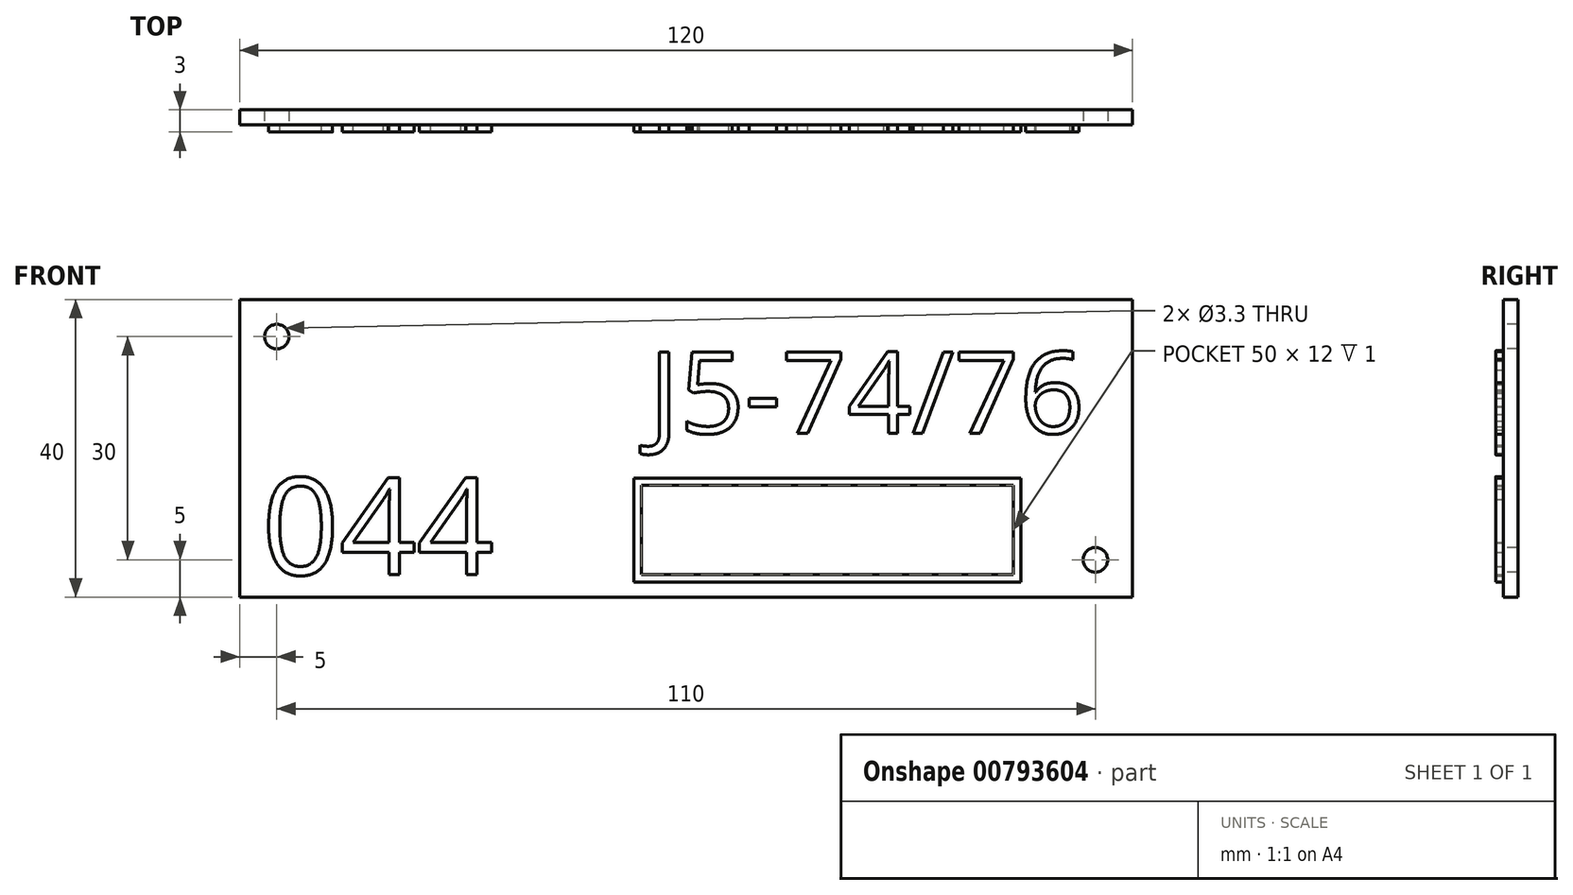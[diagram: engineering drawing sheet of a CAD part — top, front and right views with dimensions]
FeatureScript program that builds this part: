
annotation { "Feature Type Name" : "Feature", "Feature Type Description" : "" }
export const myFeature = defineFeature(function(context is Context, id is Id, definition is map)
    precondition{}
    {
        {
            var Q0;
            Q0=qCreatedBy(makeId("Front.planeOp"),FACE);
            var sketch = newSketch(context, id + "F0", { "sketchPlane" : qUnion([Q0])});
            skLineSegment(sketch, "E0.bottom", {"start": v(60, -20) * mm, "end": v(-60, -20) * mm});
            skLineSegment(sketch, "E0.top", {"start": v(60, 20) * mm, "end": v(-60, 20) * mm});
            skLineSegment(sketch, "E0.left", {"start": v(60, -20) * mm, "end": v(60, 20) * mm});
            skLineSegment(sketch, "E0.right", {"start": v(-60, -20) * mm, "end": v(-60, 20) * mm});
            skPoint(sketch, "E0.middle", {"position": v(0, 0) * mm});
            skSolve(sketch);
        }
        {
            var Q0;
            Q0=makeQuery(id+"F0.imprint","IMPRINT",FACE,{"disambiguationData":[TD([[makeQuery(id+"F0.imprint","IMPRINT",EDGE,{"derivedFrom":sQuery(id+"F0.wireOp",EDGE,"E0.bottom")}),-1.0]])]});
            extrude(context, id + "F1", {"entities" : qUnion([Q0]), "depth" : 2 * mm});
        }
        {
            var Q0;
            Q0=makeQuery(id+"F1.opExtrude","CAP_FACE",FACE,{"disambiguationData":[OSD([sQuery(id+"F0.wireOp",EDGE,"E0.bottom"),sQuery(id+"F0.wireOp",EDGE,"E0.top"),sQuery(id+"F0.wireOp",EDGE,"E0.left"),sQuery(id+"F0.wireOp",EDGE,"E0.right")])],"isStart":false});
            var sketch = newSketch(context, id + "F2", { "sketchPlane" : qUnion([Q0])});
            skPoint(sketch, "E1", {"position": v(-55, 15) * mm});
            skPoint(sketch, "E2", {"position": v(55, -15) * mm});
            skSolve(sketch);
        }
        {
            var Q0;
            Q0=sQuery(id+"F2.wireOp",VERTEX,"E1");
            var Q1;
            Q1=sQuery(id+"F2.wireOp",VERTEX,"E2");
            var Q2;
            Q2=makeQuery(id+"F1.opExtrude","SWEPT_BODY",BODY,{"disambiguationData":[OSD([sQuery(id+"F0.wireOp",EDGE,"E0.bottom"),sQuery(id+"F0.wireOp",EDGE,"E0.top"),sQuery(id+"F0.wireOp",EDGE,"E0.left"),sQuery(id+"F0.wireOp",EDGE,"E0.right")])]});
            hole(context, id + "F3", {"style" : HoleStyle.SIMPLE, "endStyle" : HoleEndStyle.THROUGH, "holeDiameter" : 3.3 * mm, "locations" : qUnion([Q0, Q1]), "scope" : qUnion([Q2]), "isTappedThrough" : true});
        }
        {
            var Q0;
            Q0=makeQuery(id+"F1.opExtrude","CAP_FACE",FACE,{"disambiguationData":[OSD([sQuery(id+"F0.wireOp",EDGE,"E0.bottom"),sQuery(id+"F0.wireOp",EDGE,"E0.top"),sQuery(id+"F0.wireOp",EDGE,"E0.left"),sQuery(id+"F0.wireOp",EDGE,"E0.right")])],"isStart":false});
            var sketch = newSketch(context, id + "F4", { "sketchPlane" : qUnion([Q0])});
            skText(sketch, "E3", { "text": "J5-74/76", "fontName": "OpenSans-Regular.ttf"});
            const initialGuessF4  = {"E3": [-0.005, 0.002, 1, 0, 0.01105]};
            skSetInitialGuess(sketch, initialGuessF4);
            skSolve(sketch);
        }
        {
            var Q0;
            Q0=qSketchRegion(id+"F4",true);
            extrude(context, id + "F5", {"entities" : qUnion([Q0]), "operationType" : NewBodyOperationType.ADD, "depth" : 1 * mm});
        }
        {
            var Q0;
            {var subQ0=sQuery(id+"F0.wireOp",EDGE,"E0.top");var subQ1=sQuery(id+"F0.wireOp",EDGE,"E0.left");var subQ2=sQuery(id+"F0.wireOp",EDGE,"E0.right");var subQ3=sQuery(id+"F0.wireOp",EDGE,"E0.bottom");Q0=makeQuery(id+"F5.boolean.opBoolean","SPLIT",FACE,{"disambiguationData":[TD([makeQuery(id+"F1.opExtrude","SWEPT_FACE",FACE,{"disambiguationData":[OSD([subQ3])]})])],"derivedFrom":makeQuery(id+"F1.opExtrude","CAP_FACE",FACE,{"disambiguationData":[OSD([subQ3,subQ0,subQ1,subQ2])],"isStart":false})});}
            var sketch = newSketch(context, id + "F6", { "sketchPlane" : qUnion([Q0])});
            skText(sketch, "E4", { "text": "044", "fontName": "OpenSans-Regular.ttf"});
            const initialGuessF6  = {"E4": [-0.057, -0.017, 1, 0, 0.0131]};
            skSetInitialGuess(sketch, initialGuessF6);
            skSolve(sketch);
        }
        {
            var Q0;
            Q0=qSketchRegion(id+"F6",true);
            extrude(context, id + "F7", {"entities" : qUnion([Q0]), "operationType" : NewBodyOperationType.ADD, "depth" : 1 * mm});
        }
        {
            var Q0;
            {var subQ46=sQuery(id+"F0.wireOp",EDGE,"E0.top");var subQ48=sQuery(id+"F0.wireOp",EDGE,"E0.left");var subQ66=sQuery(id+"F0.wireOp",EDGE,"E0.right");var subQ76=sQuery(id+"F0.wireOp",EDGE,"E0.bottom");var subQ77=makeQuery(id+"F1.opExtrude","SWEPT_FACE",FACE,{"disambiguationData":[OSD([subQ76])]});Q0=makeQuery(id+"F7.boolean.opBoolean","SPLIT",FACE,{"disambiguationData":[TD([subQ77])],"derivedFrom":makeQuery(id+"F5.boolean.opBoolean","SPLIT",FACE,{"disambiguationData":[TD([subQ77])],"derivedFrom":makeQuery(id+"F1.opExtrude","CAP_FACE",FACE,{"disambiguationData":[OSD([subQ76,subQ46,subQ48,subQ66])],"isStart":false})})});}
            var sketch = newSketch(context, id + "F8", { "sketchPlane" : qUnion([Q0])});
            skLineSegment(sketch, "E5.bottom", {"start": v(45, -18) * mm, "end": v(-7, -18) * mm});
            skLineSegment(sketch, "E5.top", {"start": v(45, -4) * mm, "end": v(-7, -4) * mm});
            skLineSegment(sketch, "E5.left", {"start": v(45, -18) * mm, "end": v(45, -4) * mm});
            skLineSegment(sketch, "E5.right", {"start": v(-7, -18) * mm, "end": v(-7, -4) * mm});
            skPoint(sketch, "E5.middle", {"position": v(19, -11) * mm});
            skLineSegment(sketch, "E6.0", {"start": v(44, -5) * mm, "end": v(-6, -5) * mm});
            skLineSegment(sketch, "E6.1", {"start": v(44, -17) * mm, "end": v(44, -5) * mm});
            skLineSegment(sketch, "E6.2", {"start": v(44, -17) * mm, "end": v(-6, -17) * mm});
            skLineSegment(sketch, "E6.3", {"start": v(-6, -17) * mm, "end": v(-6, -5) * mm});
            skSolve(sketch);
        }
        {
            var Q0;
            Q0=makeQuery(id+"F8.imprint","IMPRINT",FACE,{"disambiguationData":[TD([[makeQuery(id+"F8.imprint","IMPRINT",EDGE,{"derivedFrom":sQuery(id+"F8.wireOp",EDGE,"E5.bottom")}),-1.0]])]});
            extrude(context, id + "F9", {"entities" : qUnion([Q0]), "operationType" : NewBodyOperationType.ADD, "depth" : 1 * mm});
        }
    });
